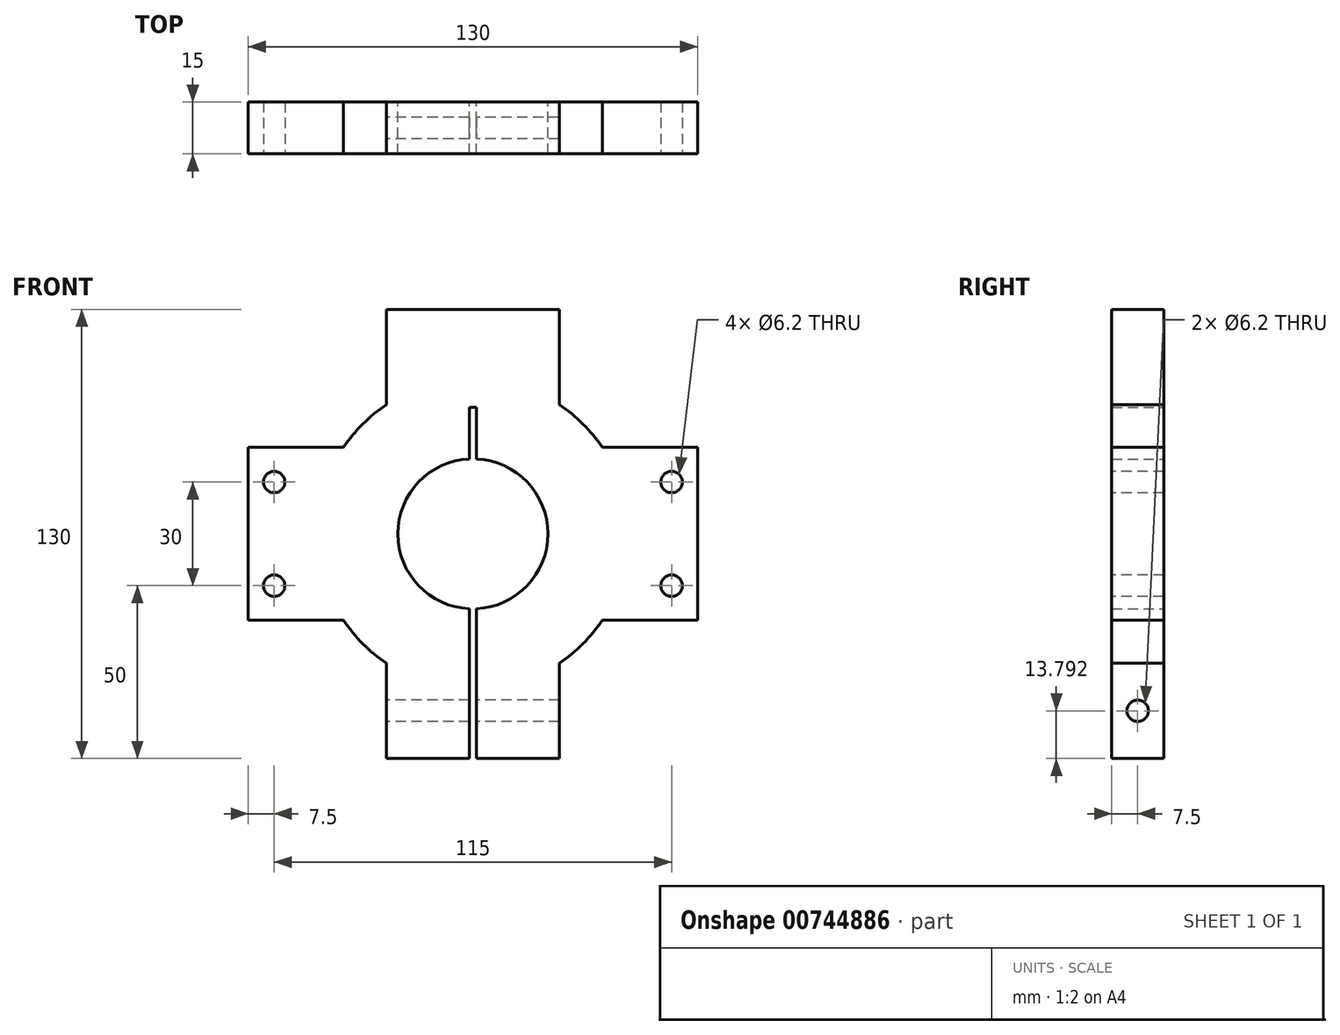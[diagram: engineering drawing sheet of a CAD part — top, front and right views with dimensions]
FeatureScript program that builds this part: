
annotation { "Feature Type Name" : "Feature", "Feature Type Description" : "" }
export const myFeature = defineFeature(function(context is Context, id is Id, definition is map)
    precondition{}
    {
        {
            var Q0;
            Q0=qCreatedBy(makeId("Front.planeOp"),FACE);
            var sketch = newSketch(context, id + "F0", { "sketchPlane" : qUnion([Q0])});
            skArc(sketch, "E0", {"start": v(37.42, 25) * mm, "mid": v(31.82, 31.82) * mm, "end": v(25, 37.42) * mm});
            skArc(sketch, "E1", {"start": v(-1, 21.68) * mm, "mid": v(-21.7, 0) * mm, "end": v(-1, -21.68) * mm});
            skLineSegment(sketch, "E2.bottom", {"start": v(25, -65) * mm, "end": v(1, -65) * mm});
            skLineSegment(sketch, "E2.top", {"start": v(25, 65) * mm, "end": v(1, 65) * mm});
            skLineSegment(sketch, "E2.left", {"start": v(25, -65) * mm, "end": v(25, -37.42) * mm});
            skLineSegment(sketch, "E2.right", {"start": v(-25, -65) * mm, "end": v(-25, -37.42) * mm});
            skLineSegment(sketch, "E3.bottom", {"start": v(65, -25) * mm, "end": v(37.42, -25) * mm});
            skLineSegment(sketch, "E3.top", {"start": v(65, 25) * mm, "end": v(37.42, 25) * mm});
            skLineSegment(sketch, "E3.left", {"start": v(65, -25) * mm, "end": v(65, 25) * mm});
            skLineSegment(sketch, "E3.right", {"start": v(-65, -25) * mm, "end": v(-65, 25) * mm});
            skLineSegment(sketch, "E4.trimOffspring", {"start": v(-25, 37.42) * mm, "end": v(-25, 65) * mm});
            skLineSegment(sketch, "E5.trimOffspring", {"start": v(-37.42, 25) * mm, "end": v(-65, 25) * mm});
            skLineSegment(sketch, "E6.trimOffspring", {"start": v(25, 37.42) * mm, "end": v(25, 65) * mm});
            skLineSegment(sketch, "E7.trimOffspring", {"start": v(-37.42, -25) * mm, "end": v(-65, -25) * mm});
            skArc(sketch, "E8.trimOffspring", {"start": v(-37.42, -25) * mm, "mid": v(-31.82, -31.82) * mm, "end": v(-25, -37.42) * mm});
            skArc(sketch, "E9.trimOffspring", {"start": v(-25, 37.42) * mm, "mid": v(-31.82, 31.82) * mm, "end": v(-37.42, 25) * mm});
            skArc(sketch, "E10.trimOffspring", {"start": v(25, -37.42) * mm, "mid": v(31.82, -31.82) * mm, "end": v(37.42, -25) * mm});
            skLineSegment(sketch, "E11.left", {"start": v(1, -65) * mm, "end": v(1, -21.68) * mm});
            skLineSegment(sketch, "E11.right", {"start": v(-1, -65) * mm, "end": v(-1, -21.68) * mm});
            skLineSegment(sketch, "E12.trimOffspring", {"start": v(-1, 65) * mm, "end": v(-25, 65) * mm});
            skPoint(sketch, "E11.top.end.orphan", {"position": v(-1, 72) * mm});
            skPoint(sketch, "E11.top.start.orphan", {"position": v(1, 72) * mm});
            skLineSegment(sketch, "E13.trimOffspring", {"start": v(-1, -65) * mm, "end": v(-25, -65) * mm});
            skPoint(sketch, "E14.orphan", {"position": v(1, -72) * mm});
            skPoint(sketch, "E15.orphan", {"position": v(-1, -72) * mm});
            skLineSegment(sketch, "E16.trimOffspring", {"start": v(1, 21.68) * mm, "end": v(1, 36.62) * mm});
            skLineSegment(sketch, "E17.trimOffspring", {"start": v(-1, 21.68) * mm, "end": v(-1, 36.62) * mm});
            skArc(sketch, "E18.trimOffspring", {"start": v(1, -21.68) * mm, "mid": v(21.7, 0) * mm, "end": v(1, 21.68) * mm});
            skLineSegment(sketch, "E19", {"start": v(-1, 36.62) * mm, "end": v(1, 36.62) * mm});
            skLineSegment(sketch, "E20", {"start": v(-1, 65) * mm, "end": v(1, 65) * mm});
            skSolve(sketch);
        }
        {
            var Q0;
            Q0 = qSketchRegion(id + "F0", true);
            extrude(context, id + "F1", {"entities" : qUnion([Q0]), "depth" : 15 * mm, "offsetDistance" : 25 * mm});
        }
        {
            var Q0;
            Q0=makeQuery(id+"F1.opExtrude","CAP_FACE",FACE,{"disambiguationData":[OSD([sQuery(id+"F0.wireOp",EDGE,"E0"),sQuery(id+"F0.wireOp",EDGE,"E1"),sQuery(id+"F0.wireOp",EDGE,"E2.bottom"),sQuery(id+"F0.wireOp",EDGE,"E2.top"),sQuery(id+"F0.wireOp",EDGE,"E2.left"),sQuery(id+"F0.wireOp",EDGE,"E2.right"),sQuery(id+"F0.wireOp",EDGE,"E3.bottom"),sQuery(id+"F0.wireOp",EDGE,"E3.top"),sQuery(id+"F0.wireOp",EDGE,"E3.left"),sQuery(id+"F0.wireOp",EDGE,"E3.right"),sQuery(id+"F0.wireOp",EDGE,"E4.trimOffspring"),sQuery(id+"F0.wireOp",EDGE,"E5.trimOffspring"),sQuery(id+"F0.wireOp",EDGE,"E6.trimOffspring"),sQuery(id+"F0.wireOp",EDGE,"E7.trimOffspring"),sQuery(id+"F0.wireOp",EDGE,"E8.trimOffspring"),sQuery(id+"F0.wireOp",EDGE,"E9.trimOffspring"),sQuery(id+"F0.wireOp",EDGE,"E10.trimOffspring"),sQuery(id+"F0.wireOp",EDGE,"E11.left"),sQuery(id+"F0.wireOp",EDGE,"E11.right"),sQuery(id+"F0.wireOp",EDGE,"E12.trimOffspring"),sQuery(id+"F0.wireOp",EDGE,"E13.trimOffspring"),sQuery(id+"F0.wireOp",EDGE,"E16.trimOffspring"),sQuery(id+"F0.wireOp",EDGE,"E17.trimOffspring"),sQuery(id+"F0.wireOp",EDGE,"E18.trimOffspring"),sQuery(id+"F0.wireOp",EDGE,"E19"),sQuery(id+"F0.wireOp",EDGE,"E20")])],"isStart":false});
            var sketch = newSketch(context, id + "F2", { "sketchPlane" : qUnion([Q0])});
            skCircle(sketch, "E21", {"center": v(57.5, 15) * mm, "radius": 3.1 * mm});
            skCircle(sketch, "E22.MirrorC", {"center": v(57.5, -15) * mm, "radius": 3.1 * mm});
            skCircle(sketch, "E23.MirrorC", {"center": v(-57.5, 15) * mm, "radius": 3.1 * mm});
            skCircle(sketch, "E24.MirrorC", {"center": v(-57.5, -15) * mm, "radius": 3.1 * mm});
            skSolve(sketch);
        }
        {
            var Q0;
            Q0 = qSketchRegion(id + "F2", true);
            extrude(context, id + "F3", {"entities" : qUnion([Q0]), "operationType" : NewBodyOperationType.REMOVE, "oppositeDirection" : true, "depth" : 25 * mm, "offsetDistance" : 25 * mm});
        }
        {
            var Q0;
            Q0=makeQuery(id+"F1.opExtrude","SWEPT_FACE",FACE,{"disambiguationData":[OSD([sQuery(id+"F0.wireOp",EDGE,"E2.right")])]});
            var sketch = newSketch(context, id + "F4", { "sketchPlane" : qUnion([Q0])});
            skCircle(sketch, "E25", {"center": v(7.5, -51.2) * mm, "radius": 3.1 * mm});
            skPoint(sketch, "E25.centerSnap0", {"position": v(15, -51.2) * mm});
            skPoint(sketch, "E25.centerSnap1", {"position": v(7.5, -65) * mm});
            skSolve(sketch);
        }
        {
            var Q0;
            Q0 = qSketchRegion(id + "F4", true);
            extrude(context, id + "F5", {"entities" : qUnion([Q0]), "operationType" : NewBodyOperationType.REMOVE, "oppositeDirection" : true, "depth" : 56.6 * mm, "offsetDistance" : 25 * mm});
        }
    });
